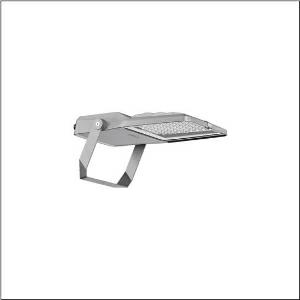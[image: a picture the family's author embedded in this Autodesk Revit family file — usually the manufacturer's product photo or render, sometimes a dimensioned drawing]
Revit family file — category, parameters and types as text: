
# Revit family: floodlight_fl_21_mini___pl61_5xa7775c2c1a_7daf
name_source: partatom
category: Lighting Fixtures
units: mm (PartAtom-declared; Revit-internal decimal feet)

## family parameters
Cut with Voids When Loaded = No
Host = Face
Light Source = No
Part Type = Normal
Room Calculation Point = No
Round Connector Dimension = Use Diameter
Shared = No

## types (1)
- --- (1 x LED, 11960 lm, 89 W, 3000K)
    Apparent Load = 89 VA
    CIE Flux Codes = 33 65 98 100 100
    Color Rendering = 70
    Color Temperature = 3000K
    Default Elevation = 1800 mm
    Description = Floodlight FL 21 mini, floodlight, primary light control with lens, of PMMA, primary optical cover: protective disc, of toughened safety glass, transparent, light distribution: PL61, light emission: direct distribution, installation type: surface-mounted, LED, High Power LED, rated luminous flux: 11.960lm, luminous efficacy: 134lm/W, light colour: 730, colour temperature: 3000K, control gear: Smart Interface (Zhaga), control: flexible luminous flux parameterisation, time-dependent luminous flux control, constant luminous flux control, overheat protection, pre-setting: logarithmic dimming characteristic, with terminal, 6-pole, mains connection: 220..240V, AC, 50/60Hz, start of lifetime: 89W, end of service life: 94W, reduction: 43W, luminaire housing, of diecast aluminium, powder-coated, SITECO metallic grey (DB 702S), corrosivity category C5 mid according to DIN EN ISO 12944, suitable for swimming pools, chlorine-resistant, sealing non-destructively replaceable, mounting bracket, of steel, galvanised, powder-coated, SITECO metallic grey (DB 702S), Smart Interface above, protection rating (complete): IP66, insulation class (complete): insulation class II (safety insulation), certification: CE, ENEC, VDE, protection symbol: D, impact resistance: IK08, permissible operating ambient temperature: -40..+40°C, permissible operating ambient temperature for outdoor applications: -40..+50°C, standard: DIN EN 12944, LABS conformity tested according to VDMA 24364:2018-05, packaging unit: 1 piece

Light Distribution: PL61
    Height = 70 mm
    Lamp = 1 x LED
    Lamp Light Flux = 11960 lm
    Lamp Power = 89 W
    Lamp count = 1
    Length = 485 mm
    Luminous efficacy = 134 lm/W
    Manufacturer = Siteco
    ModVariant = No
    Model = 5XA7775C2C1A
    Number of Poles = 1
    OnlyDefault = Yes
    Power Factor = 1
    Product Name = Floodlight FL 21 mini | PL61
    Product group = floodlight | pylon annexe
    ProductGroupID = 6201
    Protection Class = Protection class II
    Protection Degree = IP 66
    RLX_Detail_Level = 1
    RLX_Emergency_Light_Flux = 0 lm
    RLX_Emergency_Type = 0
    RLX_Emergency_Type_DB = No
    RlxData = <blob elided: 96029 chars, md5=282bf362>
    Socket = socket
    Standby Power = 0 W
    System Light Flux = 11960 lm
    System Power = 89 W
    Type Comments = factory setting: luminous flux: 100 % | dim-lin: 254 | 456 mA
    Type Image = l_1006845.jpg
    URL = http://relux.com
    VarID = @adj_171577
    Voltage = 0 V
    Weight = 0.00 kg
    Width = 337 mm

## geometry (parser evidence)
native form markers: Blend x4, Sweep x12
no freeform markers — native parametric forms only
